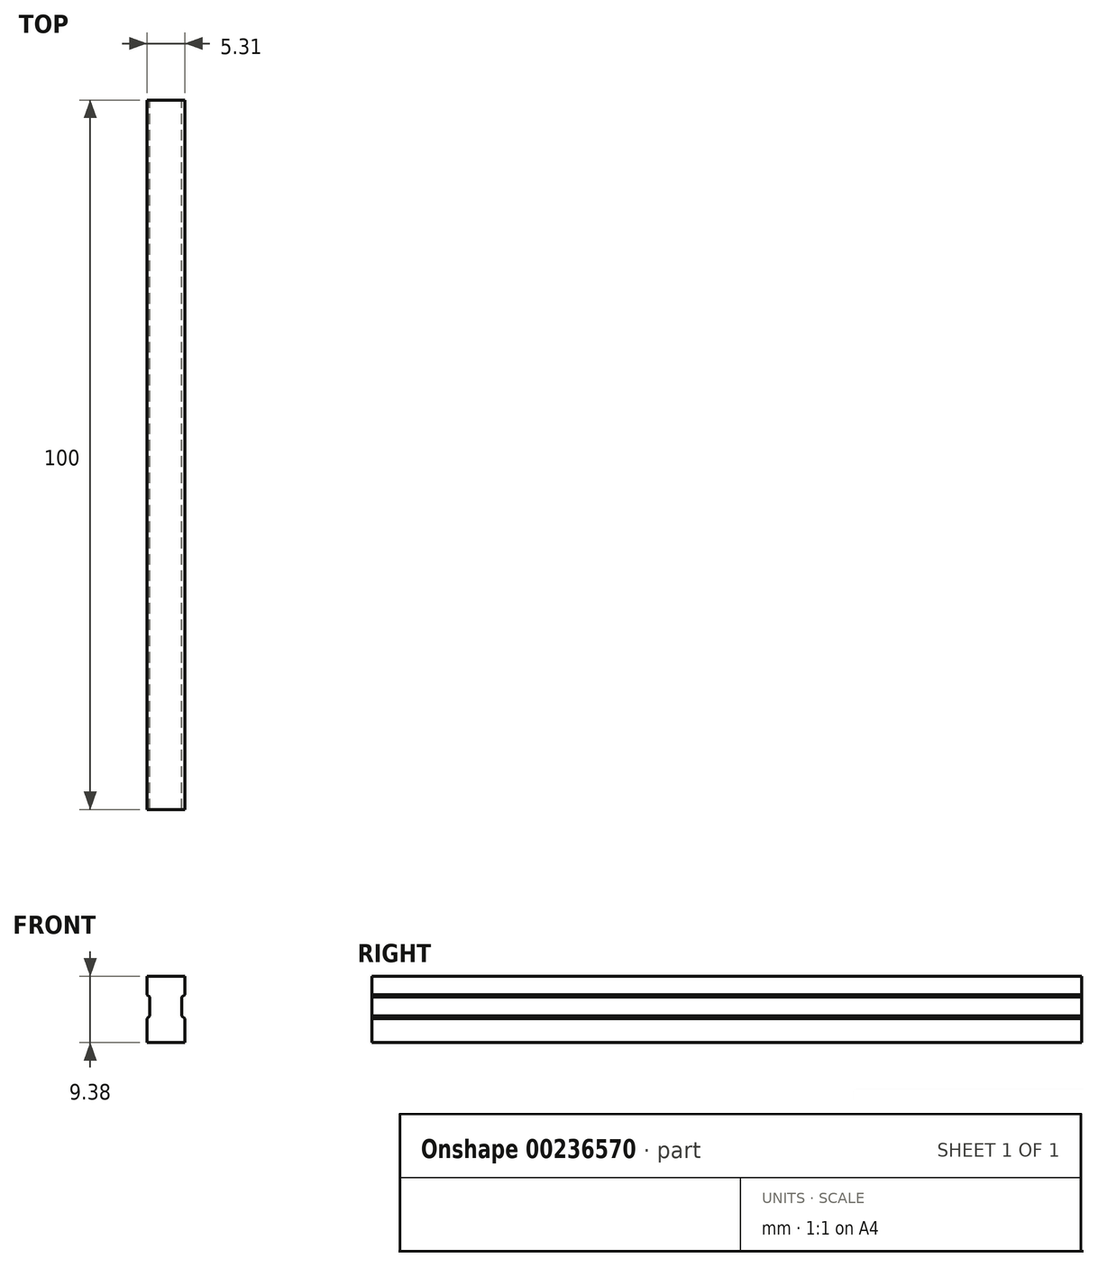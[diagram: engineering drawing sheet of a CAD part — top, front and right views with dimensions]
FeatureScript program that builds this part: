
annotation { "Feature Type Name" : "Feature", "Feature Type Description" : "" }
export const myFeature = defineFeature(function(context is Context, id is Id, definition is map)
    precondition{}
    {
        {
            var Q0;
            Q0=qCreatedBy(makeId("Front.planeOp"),FACE);
            var sketch = newSketch(context, id + "F0", { "sketchPlane" : qUnion([Q0])});
            skLineSegment(sketch, "E0.bottom", {"start": v(0, 0) * mm, "end": v(5.31, 0) * mm, "construction": true});
            skLineSegment(sketch, "E0.top", {"start": v(0, 9.38) * mm, "end": v(5.31, 9.38) * mm, "construction": true});
            skLineSegment(sketch, "E0.left", {"start": v(0, 0) * mm, "end": v(0, 9.38) * mm, "construction": true});
            skLineSegment(sketch, "E0.right", {"start": v(5.31, 0) * mm, "end": v(5.31, 9.38) * mm, "construction": true});
            skLineSegment(sketch, "E1", {"start": v(2.66, 9.38) * mm, "end": v(2.66, 0) * mm, "construction": true});
            skLineSegment(sketch, "E2", {"start": v(2.66, 0) * mm, "end": v(0, 0) * mm});
            skLineSegment(sketch, "E3", {"start": v(0, 3.4) * mm, "end": v(0.4, 3.78) * mm});
            skLineSegment(sketch, "E4", {"start": v(0.4, 3.78) * mm, "end": v(0.4, 6.4) * mm});
            skLineSegment(sketch, "E5", {"start": v(0.4, 6.4) * mm, "end": v(0, 6.78) * mm});
            skLineSegment(sketch, "E6", {"start": v(0, 6.78) * mm, "end": v(0, 9.38) * mm});
            skLineSegment(sketch, "E7", {"start": v(2.66, 9.38) * mm, "end": v(0, 9.38) * mm});
            skLineSegment(sketch, "E8", {"start": v(0, 0) * mm, "end": v(0, 3.4) * mm});
            skLineSegment(sketch, "E9.MirrorCS", {"start": v(4.9, 6.4) * mm, "end": v(5.31, 6.78) * mm});
            skLineSegment(sketch, "E10.MirrorCS", {"start": v(5.31, 3.4) * mm, "end": v(4.9, 3.78) * mm});
            skLineSegment(sketch, "E11.MirrorCS", {"start": v(5.31, 0) * mm, "end": v(5.31, 3.4) * mm});
            skLineSegment(sketch, "E12.MirrorCS", {"start": v(2.66, 9.38) * mm, "end": v(5.31, 9.38) * mm});
            skLineSegment(sketch, "E13.MirrorCS", {"start": v(2.66, 0) * mm, "end": v(5.31, 0) * mm});
            skLineSegment(sketch, "E14.MirrorCS", {"start": v(4.9, 3.78) * mm, "end": v(4.9, 6.4) * mm});
            skLineSegment(sketch, "E15.MirrorCS", {"start": v(5.31, 6.78) * mm, "end": v(5.31, 9.38) * mm});
            skSolve(sketch);
        }
        {
            var Q0;
            Q0=makeQuery(id+"F0.imprint","IMPRINT",FACE,{"disambiguationData":[TD([[makeQuery(id+"F0.imprint","IMPRINT",EDGE,{"derivedFrom":sQuery(id+"F0.wireOp",EDGE,"E2")}),-1.0]])]});
            extrude(context, id + "F1", {"entities" : qUnion([Q0]), "depth" : 100 * mm});
        }
    });
